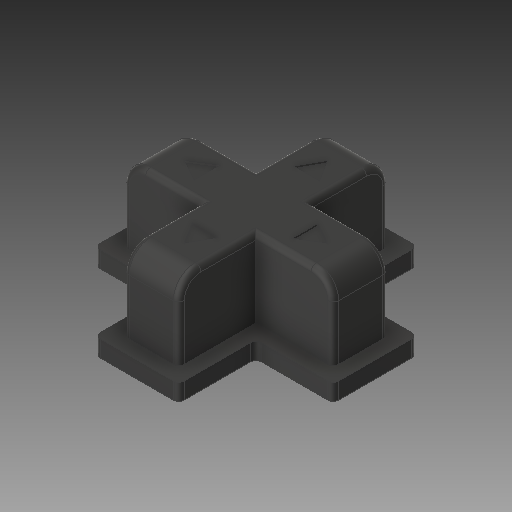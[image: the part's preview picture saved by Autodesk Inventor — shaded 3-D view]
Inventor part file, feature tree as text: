
AUTODESK INVENTOR PART (.ipt)
format: ipt  version: 2019 (Build 230136000, 136)  size: 250,368 bytes
history: native  units: mm
features: extrude x3, fillet x3, sketch x3, other x1
ambient origin geometry x8: Origin, YZ Plane, XZ Plane, XY Plane, X Axis, Y Axis, Z Axis, Center Point
bodies: Solide1 (feature_tree)
feature tree (10):
  other  "Cross"
  extrude  "Extrusion1"  Depth=19.0mm
  extrude  "Extrusion2"  Depth=19.0mm
  fillet  "Congé1"  Radius=5.0mm
  fillet  "Congé2"  Radius=5.0mm
  fillet  "Congé3"  Radius=7.0mm
  extrude  "Extrusion3"  Depth=7.0mm
  sketch  "Esquisse1"
  sketch  "Esquisse2"
  sketch  "Esquisse3"
